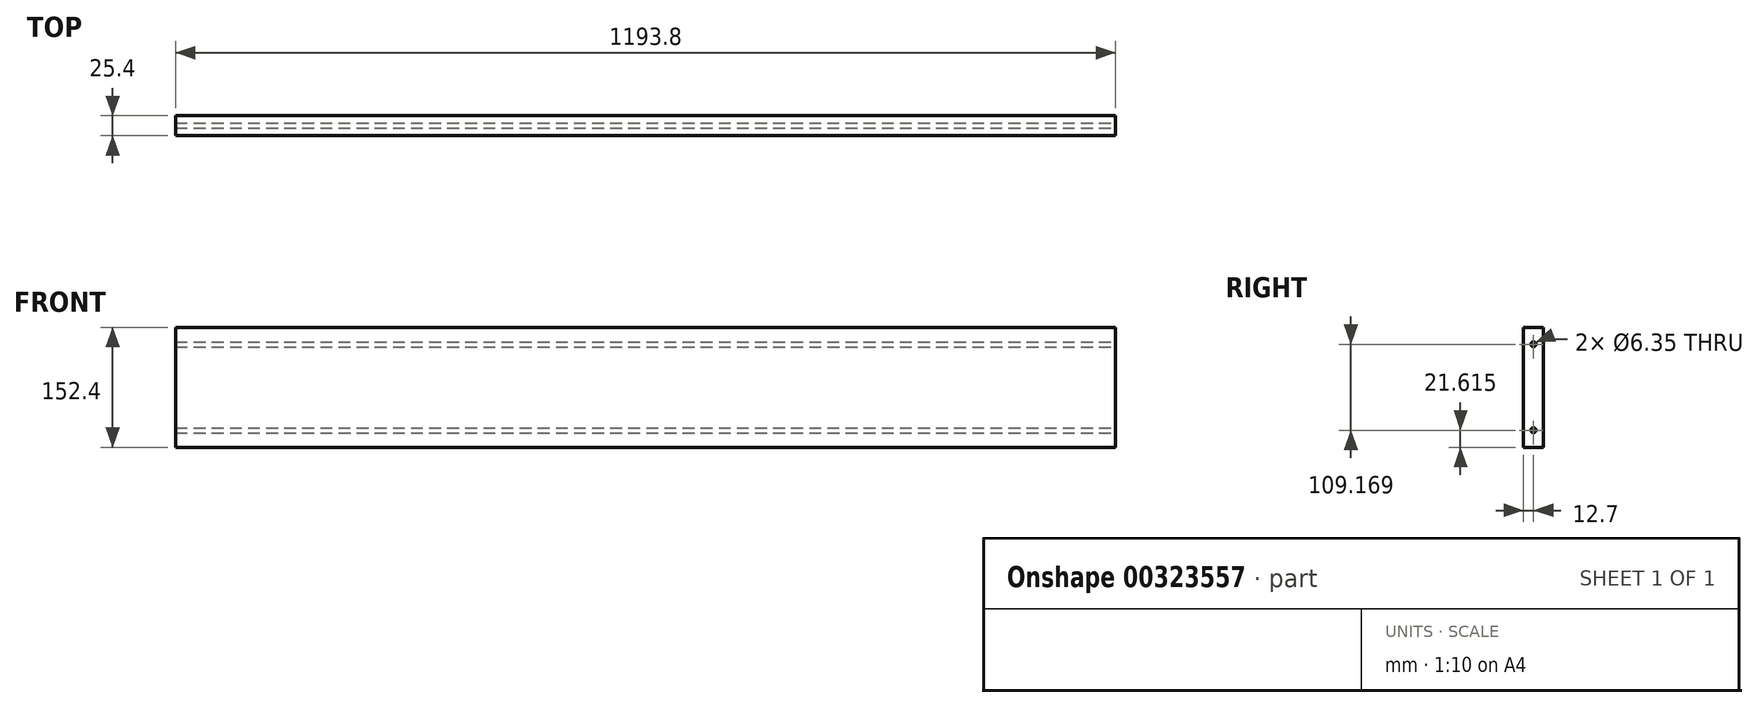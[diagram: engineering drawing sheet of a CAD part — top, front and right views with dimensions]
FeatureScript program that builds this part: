
annotation { "Feature Type Name" : "Feature", "Feature Type Description" : "" }
export const myFeature = defineFeature(function(context is Context, id is Id, definition is map)
    precondition{}
    {
        {
            var Q0;
            Q0=qCreatedBy(makeId("Front.planeOp"),FACE);
            var sketch = newSketch(context, id + "F0", { "sketchPlane" : qUnion([Q0])});
            skLineSegment(sketch, "E0.bottom", {"start": v(-596.9, 76.2) * mm, "end": v(596.9, 76.2) * mm});
            skLineSegment(sketch, "E0.top", {"start": v(-596.9, -76.2) * mm, "end": v(596.9, -76.2) * mm});
            skLineSegment(sketch, "E0.left", {"start": v(-596.9, 76.2) * mm, "end": v(-596.9, -76.2) * mm});
            skLineSegment(sketch, "E0.right", {"start": v(596.9, 76.2) * mm, "end": v(596.9, -76.2) * mm});
            skPoint(sketch, "E0.middle", {"position": v(0, 0) * mm});
            skSolve(sketch);
        }
        {
            var Q0;
            Q0 = qSketchRegion(id + "F0", true);
            extrude(context, id + "F1", {"entities" : qUnion([Q0]), "depth" : 25.4 * mm});
        }
        {
            var Q0;
            Q0=makeQuery(id+"F1.opExtrude","SWEPT_FACE",FACE,{"disambiguationData":[OSD([sQuery(id+"F0.wireOp",EDGE,"E0.right")])]});
            var sketch = newSketch(context, id + "F2", { "sketchPlane" : qUnion([Q0])});
            skPoint(sketch, "E1", {"position": v(-12.7, 0) * mm});
            skPoint(sketch, "E1.positionSnap0", {"position": v(-12.7, -76.2) * mm});
            skPoint(sketch, "E2", {"position": v(-12.7, 54.58) * mm});
            skPoint(sketch, "E3", {"position": v(-12.7, -54.58) * mm});
            skSolve(sketch);
        }
        {
            var Q0;
            Q0=sQuery(id+"F2.wireOp",VERTEX,"E2");
            var Q1;
            Q1=sQuery(id+"F2.wireOp",VERTEX,"E3");
            var Q2;
            Q2=makeQuery(id+"F1.opExtrude","SWEPT_BODY",BODY,{"disambiguationData":[OSD([sQuery(id+"F0.wireOp",EDGE,"E0.bottom"),sQuery(id+"F0.wireOp",EDGE,"E0.top"),sQuery(id+"F0.wireOp",EDGE,"E0.left"),sQuery(id+"F0.wireOp",EDGE,"E0.right")])]});
            hole(context, id + "F3", {"style" : HoleStyle.SIMPLE, "endStyle" : HoleEndStyle.THROUGH, "holeDiameter" : 6.35 * mm, "tappedDepth" : 12.7 * mm, "tapClearance" : 3, "locations" : qUnion([Q0, Q1]), "scope" : qUnion([Q2])});
        }
    });
